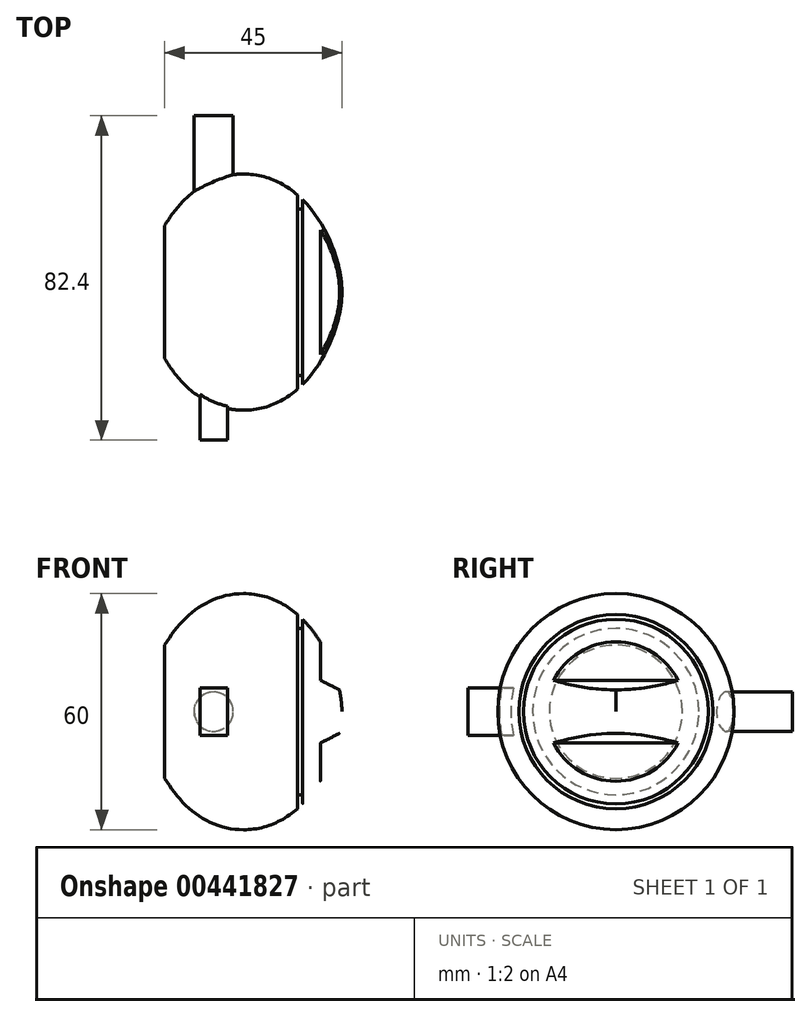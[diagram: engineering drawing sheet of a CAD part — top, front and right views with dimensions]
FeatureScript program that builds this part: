
annotation { "Feature Type Name" : "Feature", "Feature Type Description" : "" }
export const myFeature = defineFeature(function(context is Context, id is Id, definition is map)
    precondition{}
    {
        {
            var Q0;
            Q0=qCreatedBy(makeId("Front.planeOp"),FACE);
            var sketch = newSketch(context, id + "F0", { "sketchPlane" : qUnion([Q0])});
            skLineSegment(sketch, "E0", {"start": v(0, 0) * mm, "end": v(0, 30) * mm, "construction": true});
            skLineSegment(sketch, "E1", {"start": v(0, 0) * mm, "end": v(25, 0) * mm, "construction": true});
            skFitSpline(sketch, "E2", {"points": [v(0, 30) * mm, v(25, 0) * mm], "startDerivative": vector(48.78, 0) * mm, "endDerivative": vector(0, -32.98) * mm});
            skFitSpline(sketch, "E3.MirrorCS", {"points": [v(0, 30) * mm, v(-25, 0) * mm], "startDerivative": vector(-48.78, 0) * mm, "endDerivative": vector(0, -32.98) * mm});
            skLineSegment(sketch, "E4", {"start": v(-20, 16.91) * mm, "end": v(-20, 0) * mm});
            skLineSegment(sketch, "E5", {"start": v(-20, 0) * mm, "end": v(25, 0) * mm});
            skSolve(sketch);
        }
        {
            var Q0;
            Q0=qSketchRegion(id+"F0",true);
            var Q1;
            Q1=qConstructionFilter(qBodyType(qCreatedBy(id+"F0",EDGE),BodyType.WIRE),ConstructionObject.NO);
            var Q2;
            Q2=sQuery(id+"F0.wireOp",EDGE,"E1");
            revolve(context, id + "F1", {"entities" : qUnion([Q0]), "surfaceEntities" : qUnion([Q1]), "axis" : qUnion([Q2]), "revolveType" : RevolveType.FULL});
        }
        {
            var Q0;
            Q0=qCreatedBy(makeId("Front.planeOp"),FACE);
            var sketch = newSketch(context, id + "F2", { "sketchPlane" : qUnion([Q0])});
            skLineSegment(sketch, "E6", {"start": v(15.64, 0) * mm, "end": v(11.1, 0) * mm, "construction": true});
            skLineSegment(sketch, "E7", {"start": v(19.53, 19.2) * mm, "end": v(19.53, 7.97) * mm});
            skLineSegment(sketch, "E8", {"start": v(19.53, 7.97) * mm, "end": v(26.41, 4.52) * mm});
            skLineSegment(sketch, "E9", {"start": v(26.41, 4.52) * mm, "end": v(26.41, 18.83) * mm});
            skLineSegment(sketch, "E10", {"start": v(26.41, 18.83) * mm, "end": v(19.53, 19.2) * mm});
            skLineSegment(sketch, "E11.MirrorCS", {"start": v(19.53, -19.2) * mm, "end": v(19.53, -7.97) * mm});
            skLineSegment(sketch, "E12.MirrorCS", {"start": v(26.41, -4.52) * mm, "end": v(26.41, -18.83) * mm});
            skLineSegment(sketch, "E13.MirrorCS", {"start": v(19.53, -7.97) * mm, "end": v(26.41, -4.52) * mm});
            skLineSegment(sketch, "E14.MirrorCS", {"start": v(26.41, -18.83) * mm, "end": v(19.53, -19.2) * mm});
            skSolve(sketch);
        }
        {
            var Q0;
            Q0=qSketchRegion(id+"F2",true);
            extrude(context, id + "F3", {"entities" : qUnion([Q0]), "operationType" : NewBodyOperationType.REMOVE, "endBound" : BoundingType.SYMMETRIC, "oppositeDirection" : true, "depth" : 40 * mm});
        }
        {
            var Q0;
            Q0=qCreatedBy(makeId("Front.planeOp"),FACE);
            var sketch = newSketch(context, id + "F4", { "sketchPlane" : qUnion([Q0])});
            skLineSegment(sketch, "E15.bottom", {"start": v(13.7, 31.41) * mm, "end": v(15, 31.41) * mm});
            skLineSegment(sketch, "E15.top", {"start": v(13.7, 21.13) * mm, "end": v(15, 21.13) * mm});
            skLineSegment(sketch, "E15.left", {"start": v(13.7, 31.41) * mm, "end": v(13.7, 21.13) * mm});
            skLineSegment(sketch, "E15.right", {"start": v(15, 31.41) * mm, "end": v(15, 21.13) * mm});
            skLineSegment(sketch, "E16", {"start": v(3.97, 0) * mm, "end": v(11.65, 0) * mm, "construction": true});
            skSolve(sketch);
        }
        {
            var Q0;
            Q0=makeQuery(id+"F4.imprint","IMPRINT",FACE,{"disambiguationData":[TD([[makeQuery(id+"F4.imprint","IMPRINT",EDGE,{"derivedFrom":sQuery(id+"F4.wireOp",EDGE,"E15.bottom")}),-1.0]])]});
            var Q1;
            Q1=sQuery(id+"F4.wireOp",EDGE,"E16");
            var Q2;
            Q2=sQuery(id+"F4.wireOp",EDGE,"E16");
            revolve(context, id + "F5", {"operationType" : NewBodyOperationType.REMOVE, "entities" : qUnion([Q0]), "surfaceEntities" : qUnion([Q1]), "axis" : qUnion([Q2]), "revolveType" : RevolveType.FULL, "oppositeDirection" : true});
        }
        {
            var Q0;
            Q0=qCreatedBy(makeId("Front.planeOp"),FACE);
            var sketch = newSketch(context, id + "F6", { "sketchPlane" : qUnion([Q0])});
            skLineSegment(sketch, "E17.bottom", {"start": v(-11, 6) * mm, "end": v(-4, 6) * mm});
            skLineSegment(sketch, "E17.top", {"start": v(-11, -6) * mm, "end": v(-4, -6) * mm});
            skLineSegment(sketch, "E17.left", {"start": v(-11, 6) * mm, "end": v(-11, -6) * mm});
            skLineSegment(sketch, "E17.right", {"start": v(-4, 6) * mm, "end": v(-4, -6) * mm});
            skLineSegment(sketch, "E18", {"start": v(-11, 6) * mm, "end": v(-11, 28.39) * mm, "construction": true});
            skSolve(sketch);
        }
        {
            var Q0;
            Q0=qSketchRegion(id+"F6",true);
            extrude(context, id + "F7", {"entities" : qUnion([Q0]), "operationType" : NewBodyOperationType.ADD, "depth" : 37.6 * mm});
        }
        {
            var Q0;
            Q0=qCreatedBy(makeId("Front.planeOp"),FACE);
            var sketch = newSketch(context, id + "F8", { "sketchPlane" : qUnion([Q0])});
            skCircle(sketch, "E19", {"center": v(-7.6, 0) * mm, "radius": 5 * mm});
            skSolve(sketch);
        }
        {
            var Q0;
            Q0=qSketchRegion(id+"F8",true);
            extrude(context, id + "F9", {"entities" : qUnion([Q0]), "operationType" : NewBodyOperationType.ADD, "oppositeDirection" : true, "depth" : 44.8 * mm});
        }
    });
